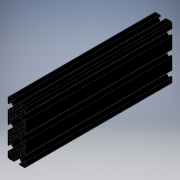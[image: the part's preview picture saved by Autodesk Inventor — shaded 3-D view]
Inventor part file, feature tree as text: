
AUTODESK INVENTOR PART (.ipt)
format: ipt  version: 2019 (Build 230136000, 136)  size: 304,640 bytes
history: native  units: mm
features: extrude x1, sketch x1
ambient origin geometry x8: Origin, YZ Plane, XZ Plane, XY Plane, X Axis, Y Axis, Z Axis, Center Point
bodies: Solid1 (feature_tree)
feature tree (2):
  extrude  "Extrusion1"  [1 undecoded]
  sketch  "Sketch_1"  dims[d0=203.2mm d1=0.0mm]
note: 1 required parameter value undecoded (feature->parameter linkage not recoverable at this tier; creation-order binding heuristic only, values carry confidence <= 0.55)
